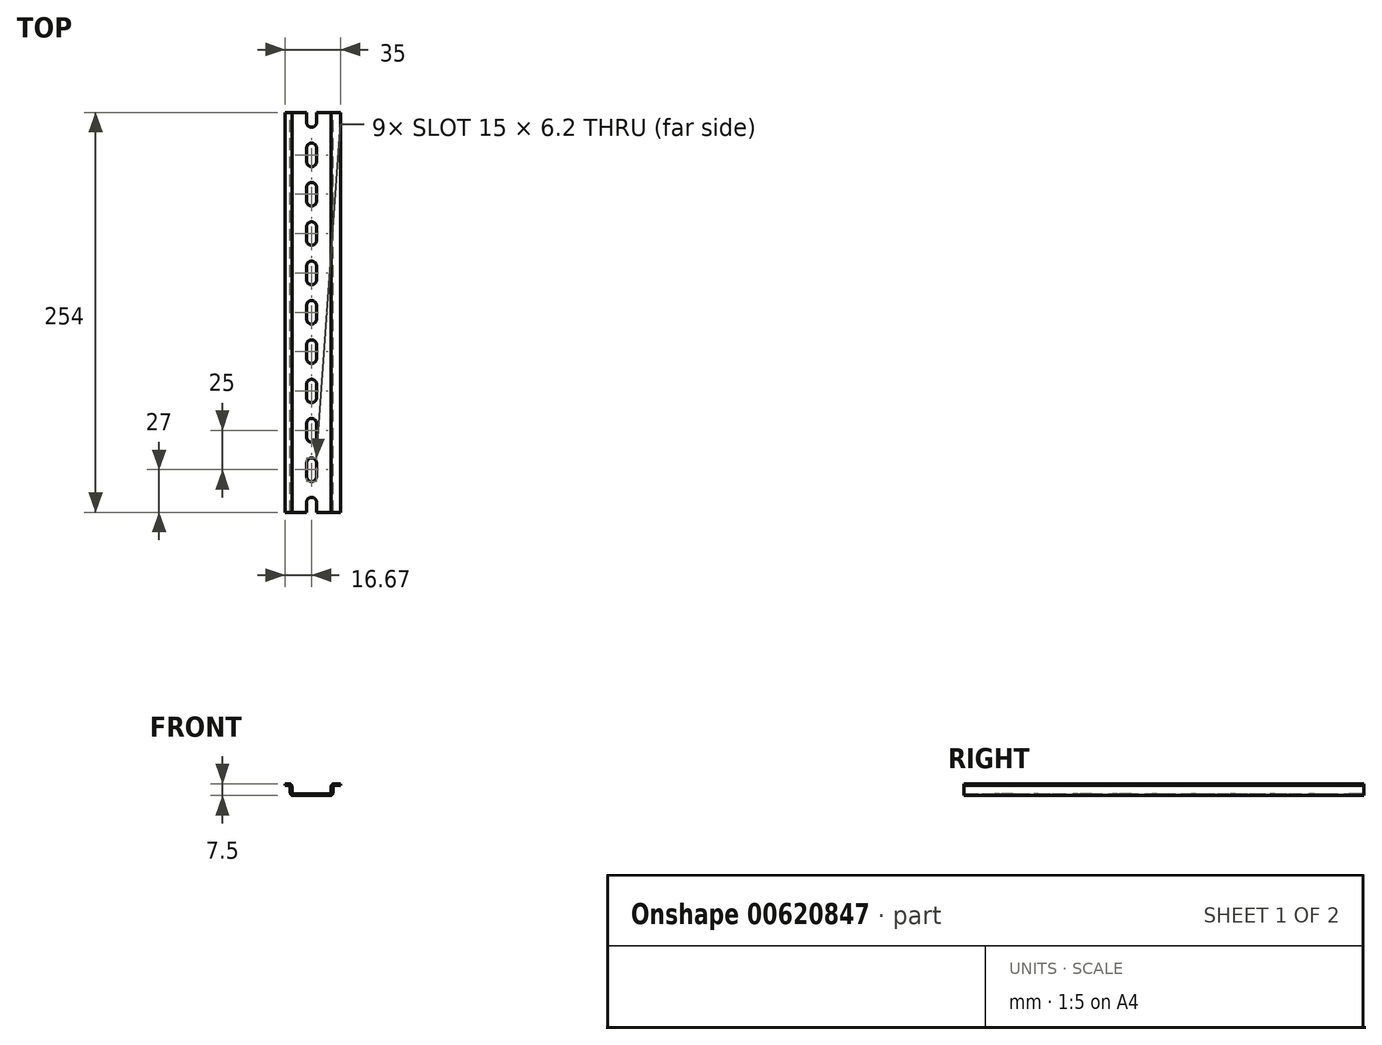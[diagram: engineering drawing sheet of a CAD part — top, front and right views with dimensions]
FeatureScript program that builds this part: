
annotation { "Feature Type Name" : "Feature", "Feature Type Description" : "" }
export const myFeature = defineFeature(function(context is Context, id is Id, definition is map)
    precondition{}
    {
        {
            var Q0;
            Q0=qCreatedBy(makeId("Front.planeOp"),FACE);
            var sketch = newSketch(context, id + "F0", { "sketchPlane" : qUnion([Q0])});
            skLineSegment(sketch, "E0", {"start": v(-11.7, 0) * mm, "end": v(11.7, 0) * mm});
            skLineSegment(sketch, "E1", {"start": v(13.5, 1.8) * mm, "end": v(13.5, 5.7) * mm});
            skLineSegment(sketch, "E2", {"start": v(14.3, 6.5) * mm, "end": v(18.33, 6.5) * mm});
            skLineSegment(sketch, "E3", {"start": v(18.33, 6.5) * mm, "end": v(18.33, 7.5) * mm});
            skLineSegment(sketch, "E4", {"start": v(18.33, 7.5) * mm, "end": v(14.3, 7.5) * mm});
            skLineSegment(sketch, "E5", {"start": v(12.5, 5.7) * mm, "end": v(12.5, 1.8) * mm});
            skLineSegment(sketch, "E6", {"start": v(11.7, 1) * mm, "end": v(-11.7, 1) * mm});
            skLineSegment(sketch, "E7", {"start": v(-12.5, 1.8) * mm, "end": v(-12.5, 5.7) * mm});
            skLineSegment(sketch, "E8", {"start": v(-14.3, 7.5) * mm, "end": v(-16.67, 7.5) * mm});
            skLineSegment(sketch, "E9", {"start": v(-16.67, 7.5) * mm, "end": v(-16.67, 6.5) * mm});
            skLineSegment(sketch, "E10", {"start": v(-16.67, 6.5) * mm, "end": v(-14.3, 6.5) * mm});
            skLineSegment(sketch, "E11", {"start": v(-13.5, 5.7) * mm, "end": v(-13.5, 1.8) * mm});
            skPoint(sketch, "E12.visualSharp", {"position": v(-12.5, 1) * mm});
            skArc(sketch, "E12.filletArc", {"start": v(-12.5, 1.8) * mm, "mid": v(-12.27, 1.23) * mm, "end": v(-11.7, 1) * mm});
            skPoint(sketch, "E13.visualSharp", {"position": v(12.5, 1) * mm});
            skArc(sketch, "E13.filletArc", {"start": v(11.7, 1) * mm, "mid": v(12.27, 1.23) * mm, "end": v(12.5, 1.8) * mm});
            skPoint(sketch, "E14.visualSharp", {"position": v(13.5, 6.5) * mm});
            skArc(sketch, "E14.filletArc", {"start": v(14.3, 6.5) * mm, "mid": v(13.73, 6.27) * mm, "end": v(13.5, 5.7) * mm});
            skPoint(sketch, "E15.visualSharp", {"position": v(-13.5, 6.5) * mm});
            skArc(sketch, "E15.filletArc", {"start": v(-13.5, 5.7) * mm, "mid": v(-13.73, 6.27) * mm, "end": v(-14.3, 6.5) * mm});
            skPoint(sketch, "E16.visualSharp", {"position": v(12.5, 7.5) * mm});
            skArc(sketch, "E16.filletArc", {"start": v(14.3, 7.5) * mm, "mid": v(13.03, 6.97) * mm, "end": v(12.5, 5.7) * mm});
            skPoint(sketch, "E17.visualSharp", {"position": v(13.5, 0) * mm});
            skArc(sketch, "E17.filletArc", {"start": v(11.7, 0) * mm, "mid": v(12.97, 0.53) * mm, "end": v(13.5, 1.8) * mm});
            skPoint(sketch, "E18.visualSharp", {"position": v(-13.5, 0) * mm});
            skArc(sketch, "E18.filletArc", {"start": v(-13.5, 1.8) * mm, "mid": v(-12.97, 0.53) * mm, "end": v(-11.7, 0) * mm});
            skPoint(sketch, "E19.visualSharp", {"position": v(-12.5, 7.5) * mm});
            skArc(sketch, "E19.filletArc", {"start": v(-12.5, 5.7) * mm, "mid": v(-13.03, 6.97) * mm, "end": v(-14.3, 7.5) * mm});
            skSolve(sketch);
        }
        {
            var Q0;
            Q0=qSketchRegion(id+"F0",true);
            extrude(context, id + "F1", {"entities" : qUnion([Q0]), "endBound" : BoundingType.SYMMETRIC, "depth" : 254 * mm, "offsetDistance" : 25 * mm});
        }
        {
            var Q0;
            Q0=makeQuery(id+"F1.opExtrude","SWEPT_FACE",FACE,{"disambiguationData":[OSD([sQuery(id+"F0.wireOp",EDGE,"E6")])]});
            var sketch = newSketch(context, id + "F2", { "sketchPlane" : qUnion([Q0])});
            skLineSegment(sketch, "E20", {"start": v(3.1, -4.4) * mm, "end": v(3.1, 4.4) * mm});
            skLineSegment(sketch, "E21", {"start": v(-3.1, 4.4) * mm, "end": v(-3.1, -4.4) * mm});
            skArc(sketch, "E22", {"start": v(3.1, 4.4) * mm, "mid": v(0, 7.5) * mm, "end": v(-3.1, 4.4) * mm});
            skArc(sketch, "E23", {"start": v(-3.1, -4.4) * mm, "mid": v(0, -7.5) * mm, "end": v(3.1, -4.4) * mm});
            skLineSegment(sketch, "E24.0.1.0", {"start": v(3.1, 20.6) * mm, "end": v(3.1, 29.4) * mm});
            skLineSegment(sketch, "E24.0.1.1", {"start": v(-3.1, 29.4) * mm, "end": v(-3.1, 20.6) * mm});
            skArc(sketch, "E24.0.1.2", {"start": v(3.1, 29.4) * mm, "mid": v(0, 32.5) * mm, "end": v(-3.1, 29.4) * mm});
            skArc(sketch, "E24.0.1.3", {"start": v(-3.1, 20.6) * mm, "mid": v(0, 17.5) * mm, "end": v(3.1, 20.6) * mm});
            skLineSegment(sketch, "E24.0.2.0", {"start": v(3.1, 45.6) * mm, "end": v(3.1, 54.4) * mm});
            skLineSegment(sketch, "E24.0.2.1", {"start": v(-3.1, 54.4) * mm, "end": v(-3.1, 45.6) * mm});
            skArc(sketch, "E24.0.2.2", {"start": v(3.1, 54.4) * mm, "mid": v(0, 57.5) * mm, "end": v(-3.1, 54.4) * mm});
            skArc(sketch, "E24.0.2.3", {"start": v(-3.1, 45.6) * mm, "mid": v(0, 42.5) * mm, "end": v(3.1, 45.6) * mm});
            skLineSegment(sketch, "E24.0.3.0", {"start": v(3.1, 70.6) * mm, "end": v(3.1, 79.4) * mm});
            skLineSegment(sketch, "E24.0.3.1", {"start": v(-3.1, 79.4) * mm, "end": v(-3.1, 70.6) * mm});
            skArc(sketch, "E24.0.3.2", {"start": v(3.1, 79.4) * mm, "mid": v(0, 82.5) * mm, "end": v(-3.1, 79.4) * mm});
            skArc(sketch, "E24.0.3.3", {"start": v(-3.1, 70.6) * mm, "mid": v(0, 67.5) * mm, "end": v(3.1, 70.6) * mm});
            skLineSegment(sketch, "E24.0.4.0", {"start": v(3.1, 95.6) * mm, "end": v(3.1, 104.4) * mm});
            skLineSegment(sketch, "E24.0.4.1", {"start": v(-3.1, 104.4) * mm, "end": v(-3.1, 95.6) * mm});
            skArc(sketch, "E24.0.4.2", {"start": v(3.1, 104.4) * mm, "mid": v(0, 107.5) * mm, "end": v(-3.1, 104.4) * mm});
            skArc(sketch, "E24.0.4.3", {"start": v(-3.1, 95.6) * mm, "mid": v(0, 92.5) * mm, "end": v(3.1, 95.6) * mm});
            skLineSegment(sketch, "E24.0.5.0", {"start": v(3.1, 120.6) * mm, "end": v(3.1, 129.4) * mm});
            skLineSegment(sketch, "E24.0.5.1", {"start": v(-3.1, 129.4) * mm, "end": v(-3.1, 120.6) * mm});
            skArc(sketch, "E24.0.5.2", {"start": v(3.1, 129.4) * mm, "mid": v(0, 132.5) * mm, "end": v(-3.1, 129.4) * mm});
            skArc(sketch, "E24.0.5.3", {"start": v(-3.1, 120.6) * mm, "mid": v(0, 117.5) * mm, "end": v(3.1, 120.6) * mm});
            skLineSegment(sketch, "E24.direction1", {"start": v(-3.1, -1.3) * mm, "end": v(21.9, -1.3) * mm, "construction": true});
            skLineSegment(sketch, "E24.direction2", {"start": v(-3.1, -4.4) * mm, "end": v(-3.1, 20.6) * mm, "construction": true});
            skArc(sketch, "E25.MirrorCS", {"start": v(3.1, -29.4) * mm, "mid": v(0, -32.5) * mm, "end": v(-3.1, -29.4) * mm});
            skArc(sketch, "E26.MirrorCS", {"start": v(-3.1, -45.6) * mm, "mid": v(0, -42.5) * mm, "end": v(3.1, -45.6) * mm});
            skArc(sketch, "E27.MirrorCS", {"start": v(3.1, -79.4) * mm, "mid": v(0, -82.5) * mm, "end": v(-3.1, -79.4) * mm});
            skArc(sketch, "E28.MirrorCS", {"start": v(-3.1, -95.6) * mm, "mid": v(0, -92.5) * mm, "end": v(3.1, -95.6) * mm});
            skArc(sketch, "E29.MirrorCS", {"start": v(-3.1, -120.6) * mm, "mid": v(0, -117.5) * mm, "end": v(3.1, -120.6) * mm});
            skLineSegment(sketch, "E30.MirrorCS", {"start": v(-3.1, -129.4) * mm, "end": v(-3.1, -120.6) * mm});
            skLineSegment(sketch, "E31.MirrorCS", {"start": v(3.1, -120.6) * mm, "end": v(3.1, -129.4) * mm});
            skLineSegment(sketch, "E32.MirrorCS", {"start": v(3.1, -45.6) * mm, "end": v(3.1, -54.4) * mm});
            skArc(sketch, "E33.MirrorCS", {"start": v(-3.1, -20.6) * mm, "mid": v(0, -17.5) * mm, "end": v(3.1, -20.6) * mm});
            skLineSegment(sketch, "E34.MirrorCS", {"start": v(3.1, -20.6) * mm, "end": v(3.1, -29.4) * mm});
            skLineSegment(sketch, "E35.MirrorCS", {"start": v(-3.1, -54.4) * mm, "end": v(-3.1, -45.6) * mm});
            skLineSegment(sketch, "E36.MirrorCS", {"start": v(-3.1, -29.4) * mm, "end": v(-3.1, -20.6) * mm});
            skLineSegment(sketch, "E37.MirrorCS", {"start": v(-3.1, -104.4) * mm, "end": v(-3.1, -95.6) * mm});
            skLineSegment(sketch, "E38.MirrorCS", {"start": v(-3.1, -79.4) * mm, "end": v(-3.1, -70.6) * mm});
            skArc(sketch, "E39.MirrorCS", {"start": v(3.1, -104.4) * mm, "mid": v(0, -107.5) * mm, "end": v(-3.1, -104.4) * mm});
            skArc(sketch, "E40.MirrorCS", {"start": v(3.1, -129.4) * mm, "mid": v(0, -132.5) * mm, "end": v(-3.1, -129.4) * mm});
            skLineSegment(sketch, "E41.MirrorCS", {"start": v(3.1, -95.6) * mm, "end": v(3.1, -104.4) * mm});
            skLineSegment(sketch, "E42.MirrorCS", {"start": v(3.1, -70.6) * mm, "end": v(3.1, -79.4) * mm});
            skArc(sketch, "E43.MirrorCS", {"start": v(-3.1, -70.6) * mm, "mid": v(0, -67.5) * mm, "end": v(3.1, -70.6) * mm});
            skArc(sketch, "E44.MirrorCS", {"start": v(3.1, -54.4) * mm, "mid": v(0, -57.5) * mm, "end": v(-3.1, -54.4) * mm});
            skSolve(sketch);
        }
        {
            var Q0;
            Q0=qSketchRegion(id+"F2",true);
            extrude(context, id + "F3", {"entities" : qUnion([Q0]), "operationType" : NewBodyOperationType.REMOVE, "endBound" : BoundingType.THROUGH_ALL, "oppositeDirection" : true, "depth" : 25.4 * mm, "offsetDistance" : 25 * mm});
        }
        {
            var Q0;
            Q0=makeQuery(id+"F2.imprint","IMPRINT",FACE,{"disambiguationData":[TD([[makeQuery(id+"F2.imprint","IMPRINT",EDGE,{"derivedFrom":sQuery(id+"F2.wireOp",EDGE,"E24.0.4.0")}),1.0]])]});
            var Q1;
            Q1=makeQuery(id+"F2.imprint","IMPRINT",FACE,{"disambiguationData":[TD([[makeQuery(id+"F2.imprint","IMPRINT",EDGE,{"derivedFrom":sQuery(id+"F2.wireOp",EDGE,"E24.0.3.0")}),1.0]])]});
            var Q2;
            Q2=makeQuery(id+"F2.imprint","IMPRINT",FACE,{"disambiguationData":[TD([[makeQuery(id+"F2.imprint","IMPRINT",EDGE,{"derivedFrom":sQuery(id+"F2.wireOp",EDGE,"E24.0.2.0")}),1.0]])]});
            var Q3;
            Q3=makeQuery(id+"F2.imprint","IMPRINT",FACE,{"disambiguationData":[TD([[makeQuery(id+"F2.imprint","IMPRINT",EDGE,{"derivedFrom":sQuery(id+"F2.wireOp",EDGE,"E24.0.1.0")}),1.0]])]});
            var Q4;
            Q4=makeQuery(id+"F2.imprint","IMPRINT",FACE,{"disambiguationData":[TD([[makeQuery(id+"F2.imprint","IMPRINT",EDGE,{"derivedFrom":sQuery(id+"F2.wireOp",EDGE,"E20")}),1.0]])]});
            var Q5;
            Q5=makeQuery(id+"F2.imprint","IMPRINT",FACE,{"disambiguationData":[TD([[makeQuery(id+"F2.imprint","IMPRINT",EDGE,{"derivedFrom":sQuery(id+"F2.wireOp",EDGE,"fe6e31e4-8ffa-49d9-9baa-646794fc51610.MirrorCS")}),-1.0]])]});
            var Q6;
            Q6=makeQuery(id+"F2.imprint","IMPRINT",FACE,{"disambiguationData":[TD([[makeQuery(id+"F2.imprint","IMPRINT",EDGE,{"derivedFrom":sQuery(id+"F2.wireOp",EDGE,"fe6e31e4-8ffa-49d9-9baa-646794fc51614.MirrorCS")}),-1.0]])]});
            var Q7;
            Q7=makeQuery(id+"F2.imprint","IMPRINT",FACE,{"disambiguationData":[TD([[makeQuery(id+"F2.imprint","IMPRINT",EDGE,{"derivedFrom":sQuery(id+"F2.wireOp",EDGE,"fe6e31e4-8ffa-49d9-9baa-646794fc51613.MirrorCS")}),-1.0]])]});
            var Q8;
            Q8=makeQuery(id+"F2.imprint","IMPRINT",FACE,{"disambiguationData":[TD([[makeQuery(id+"F2.imprint","IMPRINT",EDGE,{"derivedFrom":sQuery(id+"F2.wireOp",EDGE,"fe6e31e4-8ffa-49d9-9baa-646794fc51615.MirrorCS")}),-1.0]])]});
            var Q9;
            {var subQ0=sQuery(id+"F2.wireOp",EDGE,"fe6e31e4-8ffa-49d9-9baa-646794fc51616.MirrorCS");Q9=makeQuery(id+"F2.imprint","IMPRINT",FACE,{"disambiguationData":[TD([[makeQuery(id+"F2.imprint","IMPRINT",EDGE,{"derivedFrom":subQ0}),-1.0]])]});}
            var Q10;
            {var subQ0=sQuery(id+"F2.wireOp",EDGE,"fe6e31e4-8ffa-49d9-9baa-646794fc51611.MirrorCS");Q10=makeQuery(id+"F2.imprint","IMPRINT",FACE,{"disambiguationData":[TD([[makeQuery(id+"F2.imprint","IMPRINT",EDGE,{"derivedFrom":subQ0}),-1.0]])]});}
            var Q11;
            {var subQ0=sQuery(id+"F2.wireOp",EDGE,"E24.0.5.3");Q11=makeQuery(id+"F2.imprint","IMPRINT",FACE,{"disambiguationData":[TD([[makeQuery(id+"F2.imprint","IMPRINT",EDGE,{"derivedFrom":subQ0}),1.0]])]});}
            var Q12;
            {var subQ0=sQuery(id+"F2.wireOp",EDGE,"E24.0.5.2");Q12=makeQuery(id+"F2.imprint","IMPRINT",FACE,{"disambiguationData":[TD([[makeQuery(id+"F2.imprint","IMPRINT",EDGE,{"derivedFrom":subQ0}),1.0]])]});}
            var Q13;
            Q13=makeQuery(id+"F1.opExtrude","SWEPT_FACE",FACE,{"disambiguationData":[OSD([sQuery(id+"F0.wireOp",EDGE,"E0")])]});
            extrude(context, id + "F4", {"entities" : qUnion([Q0, Q1, Q2, Q3, Q4, Q5, Q6, Q7, Q8, Q9, Q10, Q11, Q12]), "operationType" : NewBodyOperationType.REMOVE, "endBound" : BoundingType.UP_TO_SURFACE, "oppositeDirection" : true, "depth" : 25 * mm, "endBoundEntityFace" : qUnion([Q13]), "offsetDistance" : 25 * mm});
        }
    });
